# Revit family: Plumbing Fixture-FloorDrain_Mifab_C1100-S
name_source: partatom
category: Plumbing Fixtures
revit_build: Autodesk Revit Structure 2013 (Build: 20120221_2030(x64)
units: mm (PartAtom-declared; Revit-internal decimal feet)

## types (5) — shared parameters
Body Height = 2.2 "
Floor Drain Material = Paint - Sherwin Williams Paint - #952C2A - Bellwood Red
Manufacturer = MIFAB
Model = C1100-S
Top Assembly Height = 1.25 "
URL = WWW.MIFAB.COM
zero-valued in all types: Default Elevation, WFU

## per-type parameters (varying)
| type | Description | Pipe Diameter | Pipe Radius | Stainer Diameter | Strainer Radius |
| 3" | FLOOR CLEANOUT WITH SQUARE ADJUSTABLE COVER AND PLUG
BRONZE WALL ACCESS PANEL | 3 " | 1.5 " | 8.3 " | 4.15 " |
| 2" | FLOOR CLEANOUT WITH SQUARE ADJUSTABLE COVER AND PLUG | 2 " | 1 " | 8.3 " | 4.15 " |
| 4" | FLOOR CLEANOUT WITH SQUARE ADJUSTABLE COVER AND PLUG | 4 " | 2 " | 8 " | 4 " |
| 5" | FLOOR CLEANOUT WITH SQUARE ADJUSTABLE COVER AND PLUG
BRONZE WALL ACCESS PANELLINE CLEANOUT WITH SQUARE, NICKEL
BRONZE WALL ACCESS PANELLINE CLEANOUT WITH SQUARE, NICKEL
BRONZE WALL ACCESS PANEL | 5 " | 2.5 " | 8 " | 4 " |
| 6" | FLOOR CLEANOUT WITH SQUARE ADJUSTABLE COVER AND PLUG
BRONZE WALL ACCESS PANELLINE CLEANOUT WITH SQUARE, NICKEL
BRONZE WALL ACCESS PANELLINE CLEANOUT WITH SQUARE, NICKEL
BRONZE WALL ACCESS PANEL | 6 " | 3 " | 8 " | 4 " |

## geometry (parser evidence)
native form markers: Blend x3, Sweep x1
no freeform markers — native parametric forms only
